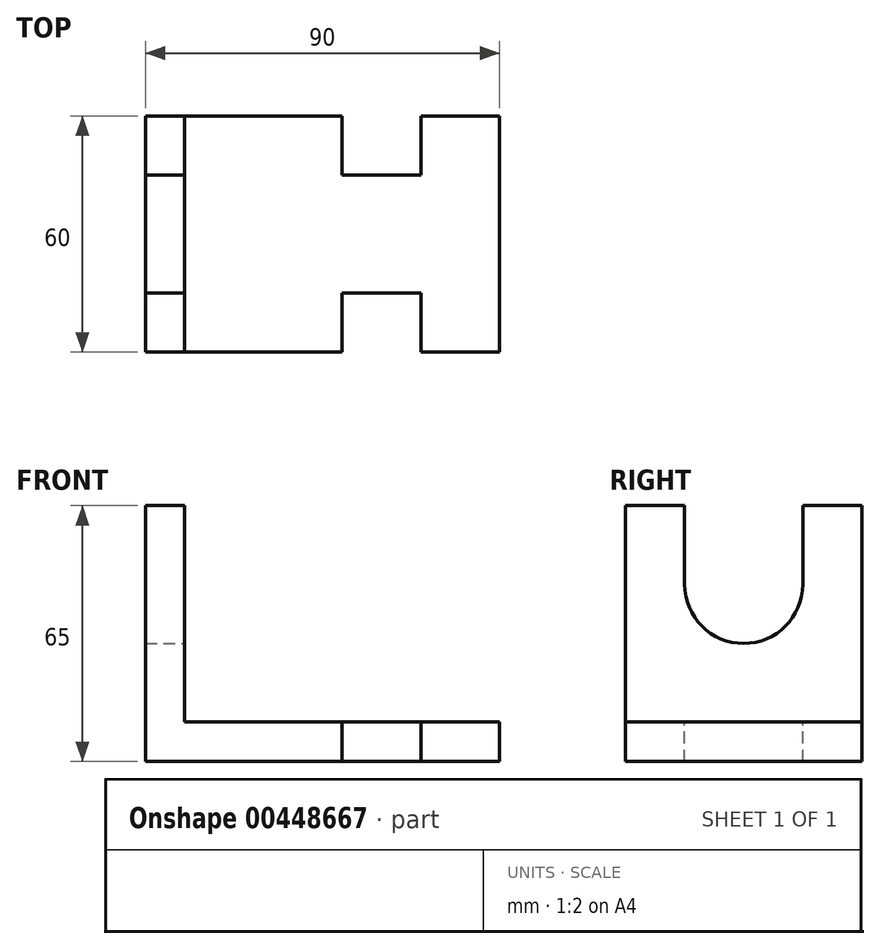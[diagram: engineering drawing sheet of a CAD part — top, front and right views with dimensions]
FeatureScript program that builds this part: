
annotation { "Feature Type Name" : "Feature", "Feature Type Description" : "" }
export const myFeature = defineFeature(function(context is Context, id is Id, definition is map)
    precondition{}
    {
        {
            var Q0;
            Q0=qCreatedBy(makeId("Front.planeOp"),FACE);
            var sketch = newSketch(context, id + "F0", { "sketchPlane" : qUnion([Q0])});
            skLineSegment(sketch, "E0.bottom", {"start": v(5, 32.5) * mm, "end": v(-5, 32.5) * mm});
            skLineSegment(sketch, "E0.top", {"start": v(5, -32.5) * mm, "end": v(-5, -32.5) * mm});
            skLineSegment(sketch, "E0.left", {"start": v(5, 32.5) * mm, "end": v(5, -22.5) * mm});
            skLineSegment(sketch, "E0.right", {"start": v(-5, 32.5) * mm, "end": v(-5, -32.5) * mm});
            skPoint(sketch, "E0.middle", {"position": v(0, 0) * mm});
            skLineSegment(sketch, "E1.bottom", {"start": v(5, -32.5) * mm, "end": v(85, -32.5) * mm});
            skLineSegment(sketch, "E1.top", {"start": v(5, -22.5) * mm, "end": v(85, -22.5) * mm});
            skLineSegment(sketch, "E1.right", {"start": v(85, -32.5) * mm, "end": v(85, -22.5) * mm});
            skSolve(sketch);
        }
        {
            var Q0;
            Q0=makeQuery(id+"F0.imprint","IMPRINT",FACE,{"disambiguationData":[TD([[makeQuery(id+"F0.imprint","IMPRINT",EDGE,{"derivedFrom":sQuery(id+"F0.wireOp",EDGE,"E0.bottom")}),1.0]])]});
            extrude(context, id + "F1", {"entities" : qUnion([Q0]), "oppositeDirection" : true, "depth" : 60 * mm});
        }
        {
            var Q0;
            Q0=makeQuery(id+"F1.opExtrude","SWEPT_FACE",FACE,{"disambiguationData":[OSD([sQuery(id+"F0.wireOp",EDGE,"E1.top")])]});
            var sketch = newSketch(context, id + "F2", { "sketchPlane" : qUnion([Q0])});
            skLineSegment(sketch, "E2.right", {"start": v(65, 0) * mm, "end": v(65, 15) * mm});
            skLineSegment(sketch, "E3.bottom", {"start": v(65, 15) * mm, "end": v(45, 15) * mm});
            skLineSegment(sketch, "E3.top", {"start": v(65, 0) * mm, "end": v(45, 0) * mm});
            skLineSegment(sketch, "E3.left", {"start": v(65, 15) * mm, "end": v(65, 0) * mm});
            skLineSegment(sketch, "E3.right", {"start": v(45, 15) * mm, "end": v(45, 0) * mm});
            skLineSegment(sketch, "E4", {"start": v(85, 30) * mm, "end": v(-16.17, 30) * mm});
            skLineSegment(sketch, "E5.MirrorCS", {"start": v(65, 60) * mm, "end": v(65, 45) * mm});
            skLineSegment(sketch, "E6.MirrorCS", {"start": v(65, 45) * mm, "end": v(45, 45) * mm});
            skLineSegment(sketch, "E7.MirrorCS", {"start": v(65, 60) * mm, "end": v(45, 60) * mm});
            skLineSegment(sketch, "E8.MirrorCS", {"start": v(45, 45) * mm, "end": v(45, 60) * mm});
            skLineSegment(sketch, "E9.MirrorCS", {"start": v(65, 45) * mm, "end": v(65, 60) * mm});
            skSolve(sketch);
        }
        {
            var Q0;
            Q0=makeQuery(id+"F2.imprint","IMPRINT",FACE,{"disambiguationData":[TD([[makeQuery(id+"F2.imprint","IMPRINT",EDGE,{"derivedFrom":sQuery(id+"F2.wireOp",EDGE,"E3.bottom")}),1.0]])]});
            var Q1;
            Q1=makeQuery(id+"F2.imprint","IMPRINT",FACE,{"disambiguationData":[TD([[makeQuery(id+"F2.imprint","IMPRINT",EDGE,{"derivedFrom":sQuery(id+"F2.wireOp",EDGE,"E6.MirrorCS")}),-1.0]])]});
            extrude(context, id + "F3", {"entities" : qUnion([Q0, Q1]), "operationType" : NewBodyOperationType.REMOVE, "oppositeDirection" : true, "depth" : 25 * mm});
        }
        {
            var Q0;
            Q0=makeQuery(id+"F1.opExtrude","SWEPT_FACE",FACE,{"disambiguationData":[OSD([sQuery(id+"F0.wireOp",EDGE,"E0.left")])]});
            var sketch = newSketch(context, id + "F4", { "sketchPlane" : qUnion([Q0])});
            skArc(sketch, "E10", {"start": v(15, 12.5) * mm, "mid": v(30, -2.5) * mm, "end": v(45, 12.5) * mm});
            skLineSegment(sketch, "E11.left", {"start": v(15, 12.5) * mm, "end": v(15, 32.5) * mm});
            skLineSegment(sketch, "E11.right", {"start": v(45, 12.5) * mm, "end": v(45, 32.5) * mm});
            skPoint(sketch, "E12.start.orphan", {"position": v(30, 32.5) * mm});
            skSolve(sketch);
        }
        {
            var Q0;
            Q0=makeQuery(id+"F4.imprint","IMPRINT",FACE,{"disambiguationData":[TD([[makeQuery(id+"F4.imprint","IMPRINT",EDGE,{"derivedFrom":sQuery(id+"F4.wireOp",EDGE,"E10")}),1.0]])]});
            extrude(context, id + "F5", {"entities" : qUnion([Q0]), "operationType" : NewBodyOperationType.REMOVE, "oppositeDirection" : true, "depth" : 25 * mm});
        }
    });
